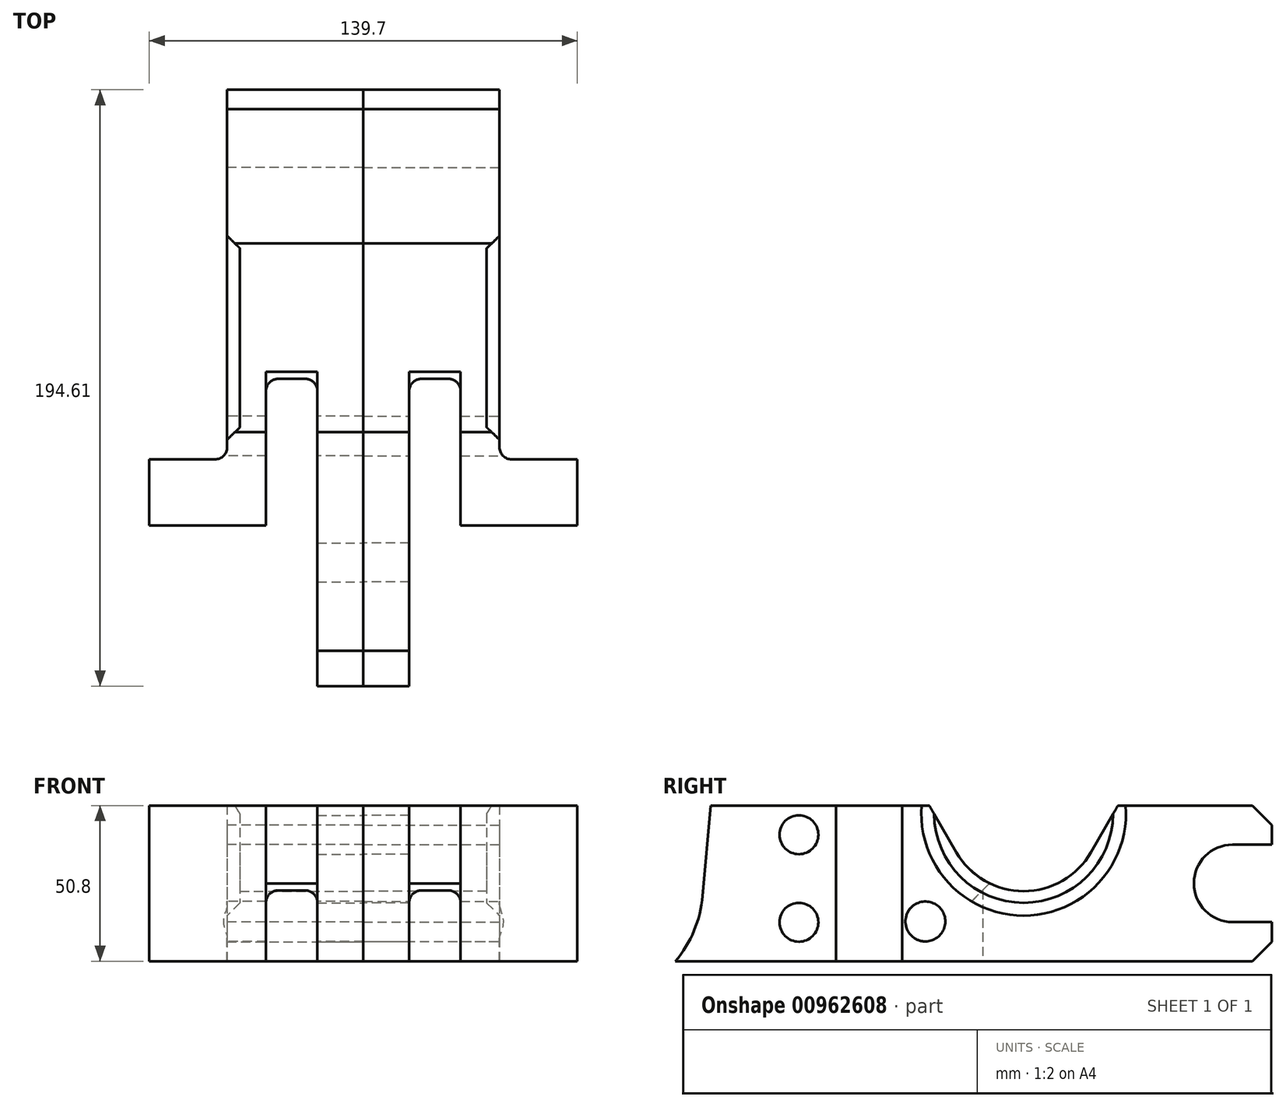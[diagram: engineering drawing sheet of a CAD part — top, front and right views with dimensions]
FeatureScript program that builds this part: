
annotation { "Feature Type Name" : "Feature", "Feature Type Description" : "" }
export const myFeature = defineFeature(function(context is Context, id is Id, definition is map)
    precondition{}
    {
        {
            var Q0;
            Q0=qCreatedBy(makeId("Top.planeOp"),FACE);
            var sketch = newSketch(context, id + "F0", { "sketchPlane" : qUnion([Q0])});
            skLineSegment(sketch, "E0.top", {"start": v(0, 120.65) * mm, "end": v(44.45, 120.65) * mm});
            skLineSegment(sketch, "E0.left", {"start": v(0, 0) * mm, "end": v(0, 120.65) * mm});
            skLineSegment(sketch, "E0.right", {"start": v(44.45, 0) * mm, "end": v(44.45, 120.65) * mm});
            skLineSegment(sketch, "E1.bottom", {"start": v(44.45, 0) * mm, "end": v(69.85, 0) * mm});
            skLineSegment(sketch, "E1.top", {"start": v(31.75, -21.6) * mm, "end": v(69.85, -21.6) * mm});
            skLineSegment(sketch, "E1.left", {"start": v(0, 0) * mm, "end": v(0, -21.6) * mm});
            skLineSegment(sketch, "E1.right", {"start": v(69.85, 0) * mm, "end": v(69.85, -21.6) * mm});
            skLineSegment(sketch, "E2.top", {"start": v(0, -73.96) * mm, "end": v(14.99, -73.96) * mm});
            skLineSegment(sketch, "E2.left", {"start": v(0, -21.6) * mm, "end": v(0, -73.96) * mm});
            skLineSegment(sketch, "E3", {"start": v(14.99, 26.28) * mm, "end": v(31.75, 26.28) * mm});
            skLineSegment(sketch, "E4", {"start": v(31.75, 26.28) * mm, "end": v(31.75, -21.6) * mm});
            skLineSegment(sketch, "E5", {"start": v(14.99, 26.28) * mm, "end": v(14.99, -73.96) * mm});
            skSolve(sketch);
        }
        {
            var Q0;
            Q0=makeQuery(id+"F0.imprint","IMPRINT",FACE,{"disambiguationData":[TD([[makeQuery(id+"F0.imprint","IMPRINT",EDGE,{"derivedFrom":sQuery(id+"F0.wireOp",EDGE,"E0.top")}),-1.0]])]});
            extrude(context, id + "F1", {"entities" : qUnion([Q0]), "depth" : 50.8 * mm, "offsetDistance" : 25.4 * mm});
        }
        {
            var Q0;
            Q0=makeQuery(id+"F1.opExtrude","SWEPT_EDGE",EDGE,{"disambiguationData":[OSD([sQuery(id+"F0.wireOp",EDGE,"E0.right"),sQuery(id+"F0.wireOp",EDGE,"E1.bottom")])]});
            var Q1;
            Q1=makeQuery(id+"F1.opExtrude","SWEPT_EDGE",EDGE,{"disambiguationData":[OSD([sQuery(id+"F0.wireOp",EDGE,"E3"),sQuery(id+"F0.wireOp",EDGE,"E5")])]});
            var Q2;
            Q2=makeQuery(id+"F1.opExtrude","SWEPT_EDGE",EDGE,{"disambiguationData":[OSD([sQuery(id+"F0.wireOp",EDGE,"E3"),sQuery(id+"F0.wireOp",EDGE,"E4")])]});
            fillet(context, id + "F2", {"entities" : qUnion([Q0, Q1, Q2]), "radius" : 3.96 * mm, "tangentPropagation" : true, "allowEdgeOverflow" : false});
        }
        {
            var Q0;
            Q0=makeQuery(id+"F1.opExtrude","CAP_EDGE",EDGE,{"disambiguationData":[OSD([sQuery(id+"F0.wireOp",EDGE,"E0.top")])],"isStart":false});
            var Q1;
            Q1=makeQuery(id+"F1.opExtrude","CAP_EDGE",EDGE,{"disambiguationData":[OSD([sQuery(id+"F0.wireOp",EDGE,"E0.top")])],"isStart":true});
            chamfer(context, id + "F3", {"entities" : qUnion([Q0, Q1]), "width" : 6.35 * mm, "tangentPropagation" : true});
        }
        {
            var Q0;
            Q0=makeQuery(id+"F1.opExtrude","SWEPT_FACE",FACE,{"disambiguationData":[OSD([sQuery(id+"F0.wireOp",EDGE,"E0.right")])]});
            var sketch = newSketch(context, id + "F4", { "sketchPlane" : qUnion([Q0])});
            skLineSegment(sketch, "E6.bottom", {"start": v(107.89, 38.04) * mm, "end": v(120.65, 38.04) * mm});
            skLineSegment(sketch, "E6.top", {"start": v(107.89, 12.76) * mm, "end": v(120.65, 12.76) * mm});
            skLineSegment(sketch, "E6.right", {"start": v(120.65, 38.04) * mm, "end": v(120.65, 12.76) * mm});
            skArc(sketch, "E7", {"start": v(107.89, 38.04) * mm, "mid": v(95.25, 25.4) * mm, "end": v(107.89, 12.76) * mm});
            skLineSegment(sketch, "E8", {"start": v(-73.96, 25.4) * mm, "end": v(120.65, 25.4) * mm, "construction": true});
            skPoint(sketch, "E9", {"position": v(95.25, 25.4) * mm});
            skSolve(sketch);
        }
        {
            var Q0;
            Q0=qSketchRegion(id+"F4",true);
            extrude(context, id + "F5", {"entities" : qUnion([Q0]), "operationType" : NewBodyOperationType.REMOVE, "endBound" : BoundingType.THROUGH_ALL, "oppositeDirection" : true, "depth" : 25.4 * mm, "offsetDistance" : 25.4 * mm});
        }
        {
            var Q0;
            Q0=makeQuery(id+"F1.opExtrude","SWEPT_FACE",FACE,{"disambiguationData":[OSD([sQuery(id+"F0.wireOp",EDGE,"E1.right")])]});
            var sketch = newSketch(context, id + "F6", { "sketchPlane" : qUnion([Q0])});
            skPoint(sketch, "E10", {"position": v(7.62, 12.95) * mm});
            skSolve(sketch);
        }
        {
            var Q0;
            Q0=sQuery(id+"F6.wireOp",VERTEX,"E10");
            var Q1;
            Q1=makeQuery(id+"F1.opExtrude","SWEPT_BODY",BODY,{"disambiguationData":[OSD([sQuery(id+"F0.wireOp",EDGE,"E0.top"),sQuery(id+"F0.wireOp",EDGE,"E0.left"),sQuery(id+"F0.wireOp",EDGE,"E0.right"),sQuery(id+"F0.wireOp",EDGE,"E1.bottom"),sQuery(id+"F0.wireOp",EDGE,"E1.top"),sQuery(id+"F0.wireOp",EDGE,"E1.left"),sQuery(id+"F0.wireOp",EDGE,"E1.right"),sQuery(id+"F0.wireOp",EDGE,"E2.top"),sQuery(id+"F0.wireOp",EDGE,"E2.left"),sQuery(id+"F0.wireOp",EDGE,"E3"),sQuery(id+"F0.wireOp",EDGE,"E4"),sQuery(id+"F0.wireOp",EDGE,"E5")])]});
            hole(context, id + "F7", {"style" : HoleStyle.SIMPLE, "endStyle" : HoleEndStyle.THROUGH, "holeDiameter" : 13.03 * mm, "majorDiameter" : 6.35 * mm, "isTappedThrough" : true, "tappedDepth" : 12.7 * mm, "tapClearance" : 3, "startFromSketch" : true, "locations" : qUnion([Q0]), "scope" : qUnion([Q1])});
        }
        {
            var Q0;
            Q0=makeQuery(id+"F1.opExtrude","SWEPT_FACE",FACE,{"disambiguationData":[OSD([sQuery(id+"F0.wireOp",EDGE,"E0.left"),sQuery(id+"F0.wireOp",EDGE,"E1.left"),sQuery(id+"F0.wireOp",EDGE,"E2.left")])]});
            var sketch = newSketch(context, id + "F8", { "sketchPlane" : qUnion([Q0])});
            skLineSegment(sketch, "E11", {"start": v(-70.48, 50.8) * mm, "end": v(-61.68, 35.56) * mm});
            skLineSegment(sketch, "E12", {"start": v(-8.9, 50.8) * mm, "end": v(-17.7, 35.56) * mm});
            skArc(sketch, "E13", {"start": v(-61.68, 35.56) * mm, "mid": v(-39.69, 22.86) * mm, "end": v(-17.7, 35.56) * mm});
            skPoint(sketch, "E13.first.point", {"position": v(-61.68, 35.56) * mm});
            skPoint(sketch, "E13.second.point", {"position": v(-17.7, 35.56) * mm});
            skPoint(sketch, "E14.orphan", {"position": v(-52.89, 20.32) * mm});
            skPoint(sketch, "E15.orphan", {"position": v(-26.49, 20.32) * mm});
            skLineSegment(sketch, "E16", {"start": v(-39.69, 48.26) * mm, "end": v(-39.69, 0) * mm, "construction": true});
            skPoint(sketch, "E16.endSnap0", {"position": v(-39.69, 22.86) * mm});
            skLineSegment(sketch, "E17", {"start": v(-70.48, 50.8) * mm, "end": v(-8.9, 50.8) * mm});
            skSolve(sketch);
        }
        {
            var Q0;
            Q0=qSketchRegion(id+"F8",true);
            extrude(context, id + "F9", {"entities" : qUnion([Q0]), "operationType" : NewBodyOperationType.REMOVE, "endBound" : BoundingType.THROUGH_ALL, "oppositeDirection" : true, "depth" : 25.4 * mm, "offsetDistance" : 25.4 * mm});
        }
        {
            var Q0;
            Q0=makeQuery(id+"F1.opExtrude","SWEPT_FACE",FACE,{"disambiguationData":[OSD([sQuery(id+"F0.wireOp",EDGE,"E1.right")])]});
            var sketch = newSketch(context, id + "F10", { "sketchPlane" : qUnion([Q0])});
            skCircle(sketch, "E18", {"center": v(39.69, 48.26) * mm, "radius": 29.21 * mm});
            skSolve(sketch);
        }
        {
            var Q0;
            Q0=qSketchRegion(id+"F10",true);
            extrude(context, id + "F11", {"entities" : qUnion([Q0]), "operationType" : NewBodyOperationType.REMOVE, "oppositeDirection" : true, "depth" : 29.6 * mm, "offsetDistance" : 25.4 * mm});
        }
        {
            var Q0;
            Q0=makeQuery(id+"F11.boolean.opBoolean","INTERSECT",EDGE,{"derivedFrom":[makeQuery(id+"F1.opExtrude","SWEPT_FACE",FACE,{"disambiguationData":[OSD([sQuery(id+"F0.wireOp",EDGE,"E0.right")])]}),makeQuery(id+"F11.opExtrude","SWEPT_FACE",FACE,{"disambiguationData":[OSD([sQuery(id+"F10.wireOp",EDGE,"E18")])]})]});
            chamfer(context, id + "F12", {"entities" : qUnion([Q0]), "width" : 4.2 * mm, "tangentPropagation" : true});
        }
        {
            var Q0;
            Q0=makeQuery(id+"F1.opExtrude","SWEPT_FACE",FACE,{"disambiguationData":[OSD([sQuery(id+"F0.wireOp",EDGE,"E5")])]});
            var sketch = newSketch(context, id + "F13", { "sketchPlane" : qUnion([Q0])});
            skArc(sketch, "E19", {"start": v(-73.96, 0) * mm, "mid": v(-67.87, 9.97) * mm, "end": v(-65.07, 21.31) * mm});
            skLineSegment(sketch, "E20", {"start": v(-65.07, 21.31) * mm, "end": v(-62.5, 50.8) * mm});
            skLineSegment(sketch, "E21", {"start": v(-62.5, 50.8) * mm, "end": v(-73.96, 50.8) * mm});
            skLineSegment(sketch, "E22", {"start": v(-73.96, 50.8) * mm, "end": v(-73.96, 0) * mm});
            skSolve(sketch);
        }
        {
            var Q0;
            Q0=qSketchRegion(id+"F13",true);
            extrude(context, id + "F14", {"entities" : qUnion([Q0]), "operationType" : NewBodyOperationType.REMOVE, "endBound" : BoundingType.THROUGH_ALL, "oppositeDirection" : true, "depth" : 25.4 * mm, "offsetDistance" : 25.4 * mm});
        }
        {
            var Q0;
            Q0=makeQuery(id+"F1.opExtrude","SWEPT_FACE",FACE,{"disambiguationData":[OSD([sQuery(id+"F0.wireOp",EDGE,"E5")])]});
            var sketch = newSketch(context, id + "F15", { "sketchPlane" : qUnion([Q0])});
            skPoint(sketch, "E23", {"position": v(26.28, 26.69) * mm});
            skLineSegment(sketch, "E24", {"start": v(26.28, 26.69) * mm, "end": v(19.26, 19.67) * mm, "construction": true});
            skLineSegment(sketch, "E25", {"start": v(22.86, 19.67) * mm, "end": v(11.93, 19.67) * mm});
            skLineSegment(sketch, "E26", {"start": v(11.93, 19.67) * mm, "end": v(11.93, 38.74) * mm});
            skLineSegment(sketch, "E27", {"start": v(11.93, 38.74) * mm, "end": v(41.92, 38.74) * mm});
            skLineSegment(sketch, "E28", {"start": v(26.28, 26.69) * mm, "end": v(38.33, 38.74) * mm, "construction": true});
            skLineSegment(sketch, "E29.0", {"start": v(22.86, 19.67) * mm, "end": v(41.92, 38.74) * mm});
            skSolve(sketch);
        }
        {
            var Q0;
            Q0=qSketchRegion(id+"F15",true);
            var Q1;
            Q1=makeQuery(id+"F1.opExtrude","SWEPT_FACE",FACE,{"disambiguationData":[OSD([sQuery(id+"F0.wireOp",EDGE,"E4")])]});
            extrude(context, id + "F16", {"entities" : qUnion([Q0]), "operationType" : NewBodyOperationType.REMOVE, "endBound" : BoundingType.UP_TO_SURFACE, "depth" : 25.4 * mm, "endBoundEntityFace" : qUnion([Q1]), "offsetDistance" : 25.4 * mm});
        }
        {
            var Q0;
            Q0=makeQuery(id+"F1.opExtrude","SWEPT_FACE",FACE,{"disambiguationData":[OSD([sQuery(id+"F0.wireOp",EDGE,"E0.left"),sQuery(id+"F0.wireOp",EDGE,"E1.left"),sQuery(id+"F0.wireOp",EDGE,"E2.left")])]});
            var sketch = newSketch(context, id + "F17", { "sketchPlane" : qUnion([Q0])});
            skCircle(sketch, "E30", {"center": v(33.65, 12.7) * mm, "radius": 6.35 * mm});
            skPoint(sketch, "E31", {"position": v(-7.62, 12.95) * mm});
            skCircle(sketch, "E32", {"center": v(33.65, 41.28) * mm, "radius": 6.35 * mm});
            skSolve(sketch);
        }
        {
            var Q0;
            Q0=qSketchRegion(id+"F17",true);
            extrude(context, id + "F18", {"entities" : qUnion([Q0]), "operationType" : NewBodyOperationType.REMOVE, "endBound" : BoundingType.THROUGH_ALL, "oppositeDirection" : true, "depth" : 25.4 * mm, "offsetDistance" : 25.4 * mm});
        }
        {
            var Q0;
            Q0=makeQuery(id+"F1.opExtrude","SWEPT_BODY",BODY,{"disambiguationData":[OSD([sQuery(id+"F0.wireOp",EDGE,"E0.top"),sQuery(id+"F0.wireOp",EDGE,"E0.left"),sQuery(id+"F0.wireOp",EDGE,"E0.right"),sQuery(id+"F0.wireOp",EDGE,"E1.bottom"),sQuery(id+"F0.wireOp",EDGE,"E1.top"),sQuery(id+"F0.wireOp",EDGE,"E1.left"),sQuery(id+"F0.wireOp",EDGE,"E1.right"),sQuery(id+"F0.wireOp",EDGE,"E2.top"),sQuery(id+"F0.wireOp",EDGE,"E2.left"),sQuery(id+"F0.wireOp",EDGE,"E3"),sQuery(id+"F0.wireOp",EDGE,"E4"),sQuery(id+"F0.wireOp",EDGE,"E5")])]});
            var Q1;
            Q1=qCreatedBy(makeId("Right.planeOp"),FACE);
            mirror(context, id + "F19", {"entities" : qUnion([Q0]), "mirrorPlane" : qUnion([Q1])});
        }
    });
